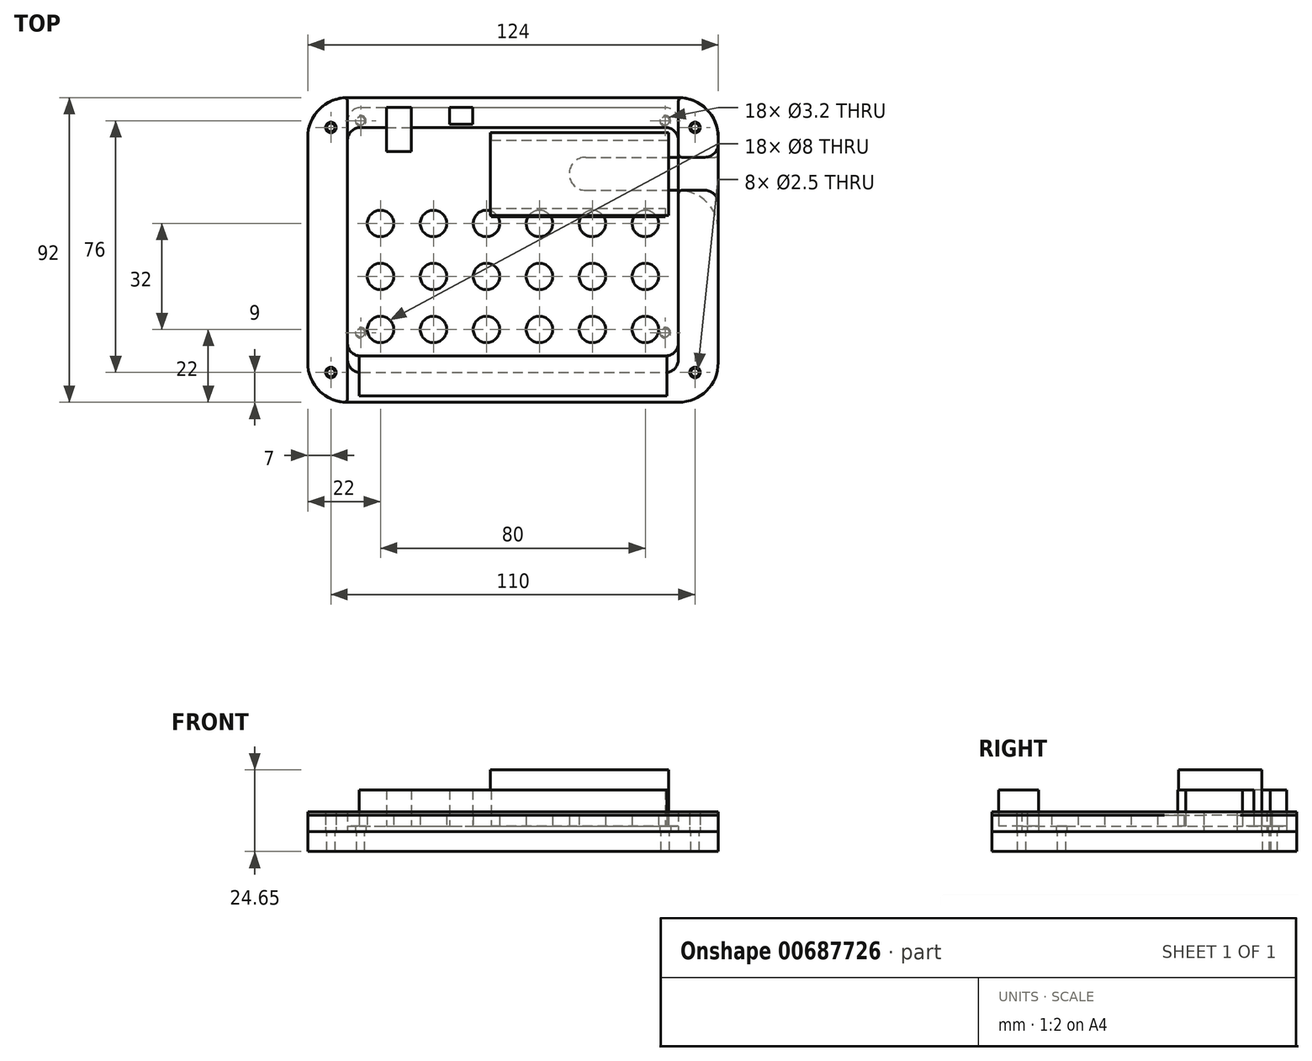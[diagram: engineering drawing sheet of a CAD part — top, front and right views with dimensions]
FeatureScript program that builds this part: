
annotation { "Feature Type Name" : "Feature", "Feature Type Description" : "" }
export const myFeature = defineFeature(function(context is Context, id is Id, definition is map)
    precondition{}
    {
        {
            var Q0;
            Q0=qCreatedBy(makeId("Top.planeOp"),FACE);
            var sketch = newSketch(context, id + "F0", { "sketchPlane" : qUnion([Q0])});
            skLineSegment(sketch, "E0.bottom", {"start": v(0, 0) * mm, "end": v(100, 0) * mm});
            skLineSegment(sketch, "E0.top", {"start": v(0, 80) * mm, "end": v(100, 80) * mm});
            skLineSegment(sketch, "E0.left", {"start": v(0, 0) * mm, "end": v(0, 80) * mm});
            skLineSegment(sketch, "E0.right", {"start": v(100, 0) * mm, "end": v(100, 80) * mm});
            skCircle(sketch, "E1", {"center": v(4, 76) * mm, "radius": 1.6 * mm});
            skCircle(sketch, "E2", {"center": v(4, 12) * mm, "radius": 1.6 * mm});
            skCircle(sketch, "E3", {"center": v(96, 76) * mm, "radius": 1.6 * mm});
            skCircle(sketch, "E4", {"center": v(96, 12) * mm, "radius": 1.6 * mm});
            skSolve(sketch);
        }
        {
            var Q0;
            Q0=makeQuery(id+"F0.imprint","IMPRINT",FACE,{"disambiguationData":[TD([[makeQuery(id+"F0.imprint","IMPRINT",EDGE,{"derivedFrom":sQuery(id+"F0.wireOp",EDGE,"E0.bottom")}),1.0]])]});
            extrude(context, id + "F1", {"entities" : qUnion([Q0]), "depth" : 1.65 * mm, "offsetDistance" : 25 * mm});
        }
        {
            var Q0;
            Q0=makeQuery(id+"F1.opExtrude","SWEPT_EDGE",EDGE,{"disambiguationData":[OSD([sQuery(id+"F0.wireOp",EDGE,"E0.top"),sQuery(id+"F0.wireOp",EDGE,"E0.left")])]});
            var Q1;
            Q1=makeQuery(id+"F1.opExtrude","SWEPT_EDGE",EDGE,{"disambiguationData":[OSD([sQuery(id+"F0.wireOp",EDGE,"E0.top"),sQuery(id+"F0.wireOp",EDGE,"E0.right")])]});
            var Q2;
            Q2=makeQuery(id+"F1.opExtrude","SWEPT_EDGE",EDGE,{"disambiguationData":[OSD([sQuery(id+"F0.wireOp",EDGE,"E0.bottom"),sQuery(id+"F0.wireOp",EDGE,"E0.right")])]});
            var Q3;
            Q3=makeQuery(id+"F1.opExtrude","SWEPT_EDGE",EDGE,{"disambiguationData":[OSD([sQuery(id+"F0.wireOp",EDGE,"E0.bottom"),sQuery(id+"F0.wireOp",EDGE,"E0.left")])]});
            fillet(context, id + "F2", {"entities" : qUnion([Q0, Q1, Q2, Q3]), "radius" : 4 * mm, "tangentPropagation" : true, "allowEdgeOverflow" : false});
        }
        {
            var Q0;
            Q0=makeQuery(id+"F1.opExtrude","CAP_FACE",FACE,{"disambiguationData":[OSD([sQuery(id+"F0.wireOp",EDGE,"E0.bottom"),sQuery(id+"F0.wireOp",EDGE,"E0.top"),sQuery(id+"F0.wireOp",EDGE,"E0.left"),sQuery(id+"F0.wireOp",EDGE,"E0.right"),sQuery(id+"F0.wireOp",EDGE,"E1"),sQuery(id+"F0.wireOp",EDGE,"E2"),sQuery(id+"F0.wireOp",EDGE,"E3"),sQuery(id+"F0.wireOp",EDGE,"E4")])],"isStart":false});
            var sketch = newSketch(context, id + "F3", { "sketchPlane" : qUnion([Q0])});
            skLineSegment(sketch, "E5.bottom", {"start": v(97, 72.5) * mm, "end": v(43.4, 72.5) * mm});
            skLineSegment(sketch, "E5.top", {"start": v(97, 70.05) * mm, "end": v(43.4, 70.05) * mm});
            skLineSegment(sketch, "E5.left", {"start": v(97, 72.5) * mm, "end": v(97, 70.05) * mm});
            skLineSegment(sketch, "E5.right", {"start": v(43.4, 72.5) * mm, "end": v(43.4, 70.05) * mm});
            skLineSegment(sketch, "E6.bottom", {"start": v(43.4, 49.55) * mm, "end": v(96, 49.55) * mm});
            skLineSegment(sketch, "E6.top", {"start": v(43.4, 47.1) * mm, "end": v(96, 47.1) * mm});
            skLineSegment(sketch, "E6.left", {"start": v(43.4, 49.55) * mm, "end": v(43.4, 47.1) * mm});
            skLineSegment(sketch, "E6.right", {"start": v(96, 49.55) * mm, "end": v(96, 47.1) * mm});
            skLineSegment(sketch, "E7.bottom", {"start": v(30.9, 80) * mm, "end": v(37.8, 80) * mm});
            skLineSegment(sketch, "E7.top", {"start": v(30.9, 75) * mm, "end": v(37.8, 75) * mm});
            skLineSegment(sketch, "E7.left", {"start": v(30.9, 80) * mm, "end": v(30.9, 75) * mm});
            skLineSegment(sketch, "E7.right", {"start": v(37.8, 80) * mm, "end": v(37.8, 75) * mm});
            skLineSegment(sketch, "E8.bottom", {"start": v(11.74, 80) * mm, "end": v(19.36, 80) * mm});
            skLineSegment(sketch, "E8.top", {"start": v(11.74, 66.69) * mm, "end": v(19.36, 66.69) * mm});
            skLineSegment(sketch, "E8.left", {"start": v(11.74, 80) * mm, "end": v(11.74, 66.69) * mm});
            skLineSegment(sketch, "E8.right", {"start": v(19.36, 80) * mm, "end": v(19.36, 66.69) * mm});
            skLineSegment(sketch, "E9.bottom", {"start": v(3.5, 5) * mm, "end": v(96.5, 5) * mm});
            skLineSegment(sketch, "E9.top", {"start": v(3.5, -7) * mm, "end": v(96.5, -7) * mm});
            skLineSegment(sketch, "E9.left", {"start": v(3.5, 5) * mm, "end": v(3.5, -7) * mm});
            skLineSegment(sketch, "E9.right", {"start": v(96.5, 5) * mm, "end": v(96.5, -7) * mm});
            skSolve(sketch);
        }
        {
            var Q0;
            Q0=makeQuery(id+"F3.imprint","IMPRINT",FACE,{"disambiguationData":[TD([[makeQuery(id+"F3.imprint","IMPRINT",EDGE,{"derivedFrom":sQuery(id+"F3.wireOp",EDGE,"E8.bottom")}),-1.0]])]});
            var Q1;
            Q1=makeQuery(id+"F3.imprint","IMPRINT",FACE,{"disambiguationData":[TD([[makeQuery(id+"F3.imprint","IMPRINT",EDGE,{"derivedFrom":sQuery(id+"F3.wireOp",EDGE,"E7.bottom")}),-1.0]])]});
            var Q2;
            Q2=makeQuery(id+"F3.imprint","IMPRINT",FACE,{"disambiguationData":[TD([[makeQuery(id+"F3.imprint","IMPRINT",EDGE,{"derivedFrom":sQuery(id+"F3.wireOp",EDGE,"E5.bottom")}),1.0]])]});
            var Q3;
            Q3=makeQuery(id+"F3.imprint","IMPRINT",FACE,{"disambiguationData":[TD([[makeQuery(id+"F3.imprint","IMPRINT",EDGE,{"derivedFrom":sQuery(id+"F3.wireOp",EDGE,"E6.bottom")}),-1.0]])]});
            var Q4;
            {var subQ1=sQuery(id+"F3.wireOp",EDGE,"E9.bottom");Q4=makeQuery(id+"F3.imprint","IMPRINT",FACE,{"disambiguationData":[TD([[makeQuery(id+"F3.imprint","IMPRINT",EDGE,{"derivedFrom":subQ1}),-1.0]])]});}
            var Q5;
            {var subQ2=sQuery(id+"F3.wireOp",EDGE,"E9.top");Q5=makeQuery(id+"F3.imprint","IMPRINT",FACE,{"disambiguationData":[TD([[makeQuery(id+"F3.imprint","IMPRINT",EDGE,{"derivedFrom":subQ2}),1.0]])]});}
            extrude(context, id + "F4", {"entities" : qUnion([Q0, Q1, Q2, Q3, Q4, Q5]), "operationType" : NewBodyOperationType.ADD, "depth" : 11 * mm, "offsetDistance" : 25 * mm});
        }
        {
            var Q0;
            Q0=qCreatedBy(makeId("Top.planeOp"),FACE);
            var sketch = newSketch(context, id + "F5", { "sketchPlane" : qUnion([Q0])});
            skLineSegment(sketch, "E10.bottom", {"start": v(-12, 83) * mm, "end": v(112, 83) * mm});
            skLineSegment(sketch, "E10.top", {"start": v(-12, -9) * mm, "end": v(112, -9) * mm});
            skLineSegment(sketch, "E10.left", {"start": v(-12, 83) * mm, "end": v(-12, -9) * mm});
            skLineSegment(sketch, "E10.right", {"start": v(112, 83) * mm, "end": v(112, -9) * mm});
            skCircle(sketch, "E11", {"center": v(4, 76) * mm, "radius": 1.25 * mm});
            skCircle(sketch, "E12", {"center": v(4, 12) * mm, "radius": 1.25 * mm});
            skCircle(sketch, "E13", {"center": v(96, 12) * mm, "radius": 1.25 * mm});
            skCircle(sketch, "E14", {"center": v(96, 76) * mm, "radius": 1.25 * mm});
            skCircle(sketch, "E15", {"center": v(-5, 74) * mm, "radius": 1.25 * mm});
            skCircle(sketch, "E16", {"center": v(-5, 0) * mm, "radius": 1.25 * mm});
            skLineSegment(sketch, "E17", {"start": v(50, 83) * mm, "end": v(50, -9) * mm, "construction": true});
            skCircle(sketch, "E18.MirrorC", {"center": v(105, 0) * mm, "radius": 1.25 * mm});
            skCircle(sketch, "E19.MirrorC", {"center": v(105, 74) * mm, "radius": 1.25 * mm});
            skSolve(sketch);
        }
        {
            var Q0;
            Q0=makeQuery(id+"F5.imprint","IMPRINT",FACE,{"disambiguationData":[TD([[makeQuery(id+"F5.imprint","IMPRINT",EDGE,{"derivedFrom":sQuery(id+"F5.wireOp",EDGE,"E10.bottom")}),-1.0]])]});
            var Q1;
            Q1=qCreatedBy(makeId("Top.planeOp"),FACE);
            extrude(context, id + "F6", {"entities" : qUnion([Q0]), "oppositeDirection" : true, "depth" : 6 * mm, "endBoundEntityFace" : qUnion([Q1]), "hasOffset" : true, "offsetDistance" : 5 * mm});
        }
        {
            var Q0;
            Q0=makeQuery(id+"F6.opExtrude","SWEPT_EDGE",EDGE,{"disambiguationData":[OSD([sQuery(id+"F5.wireOp",EDGE,"E10.bottom"),sQuery(id+"F5.wireOp",EDGE,"E10.left")])]});
            var Q1;
            Q1=makeQuery(id+"F6.opExtrude","SWEPT_EDGE",EDGE,{"disambiguationData":[OSD([sQuery(id+"F5.wireOp",EDGE,"E10.top"),sQuery(id+"F5.wireOp",EDGE,"E10.left")])]});
            var Q2;
            Q2=makeQuery(id+"F6.opExtrude","SWEPT_EDGE",EDGE,{"disambiguationData":[OSD([sQuery(id+"F5.wireOp",EDGE,"E10.top"),sQuery(id+"F5.wireOp",EDGE,"E10.right")])]});
            var Q3;
            Q3=makeQuery(id+"F6.opExtrude","SWEPT_EDGE",EDGE,{"disambiguationData":[OSD([sQuery(id+"F5.wireOp",EDGE,"E10.bottom"),sQuery(id+"F5.wireOp",EDGE,"E10.right")])]});
            fillet(context, id + "F7", {"entities" : qUnion([Q0, Q1, Q2, Q3]), "radius" : 12 * mm, "tangentPropagation" : true, "allowEdgeOverflow" : false});
        }
        {
            var Q0;
            Q0=makeQuery(id+"F4.opExtrude","CAP_FACE",FACE,{"disambiguationData":[OSD([sQuery(id+"F3.wireOp",EDGE,"E5.bottom"),sQuery(id+"F3.wireOp",EDGE,"E5.top"),sQuery(id+"F3.wireOp",EDGE,"E5.left"),sQuery(id+"F3.wireOp",EDGE,"E5.right")])],"isStart":false});
            var sketch = newSketch(context, id + "F8", { "sketchPlane" : qUnion([Q0])});
            skLineSegment(sketch, "E20.bottom", {"start": v(97, 72.5) * mm, "end": v(43.24, 72.5) * mm});
            skLineSegment(sketch, "E20.top", {"start": v(97, 47.4) * mm, "end": v(43.24, 47.4) * mm});
            skLineSegment(sketch, "E20.left", {"start": v(97, 72.5) * mm, "end": v(97, 47.4) * mm});
            skLineSegment(sketch, "E20.right", {"start": v(43.24, 72.5) * mm, "end": v(43.24, 47.4) * mm});
            skSolve(sketch);
        }
        {
            var Q0;
            {var subQ3=sQuery(id+"F8.wireOp",EDGE,"E20.top");Q0=makeQuery(id+"F8.imprint","IMPRINT",FACE,{"disambiguationData":[TD([[makeQuery(id+"F8.imprint","IMPRINT",EDGE,{"derivedFrom":subQ3}),-1.0]])]});}
            var Q1;
            {var subQ4=makeQuery(id+"F4.opExtrude","CAP_EDGE",EDGE,{"disambiguationData":[OSD([sQuery(id+"F3.wireOp",EDGE,"E5.top")])],"isStart":false});Q1=makeQuery(id+"F8.imprint","IMPRINT",FACE,{"disambiguationData":[TD([[makeQuery(id+"F8.imprint","IMPRINT",EDGE,{"derivedFrom":subQ4}),-1.0]])]});}
            extrude(context, id + "F9", {"entities" : qUnion([Q0, Q1]), "operationType" : NewBodyOperationType.ADD, "depth" : 6 * mm, "offsetDistance" : 25 * mm});
        }
        {
            var Q0;
            Q0=qCreatedBy(makeId("Top.planeOp"),FACE);
            var sketch = newSketch(context, id + "F10", { "sketchPlane" : qUnion([Q0])});
            skLineSegment(sketch, "E21.bottom", {"start": v(0, 83) * mm, "end": v(-12, 83) * mm});
            skLineSegment(sketch, "E21.top", {"start": v(0, -9) * mm, "end": v(-12, -9) * mm});
            skLineSegment(sketch, "E21.left", {"start": v(0, 83) * mm, "end": v(0, -9) * mm});
            skLineSegment(sketch, "E21.right", {"start": v(-12, 83) * mm, "end": v(-12, -9) * mm});
            skCircle(sketch, "E22", {"center": v(-5, 74) * mm, "radius": 1.6 * mm});
            skCircle(sketch, "E23", {"center": v(-5, 0) * mm, "radius": 1.6 * mm});
            skSolve(sketch);
        }
        {
            var Q0;
            Q0=makeQuery(id+"F10.imprint","IMPRINT",FACE,{"disambiguationData":[TD([[makeQuery(id+"F10.imprint","IMPRINT",EDGE,{"derivedFrom":sQuery(id+"F10.wireOp",EDGE,"E21.bottom")}),1.0]])]});
            extrude(context, id + "F11", {"entities" : qUnion([Q0]), "depth" : 6 * mm, "offsetDistance" : 25 * mm});
        }
        {
            var Q0;
            Q0=makeQuery(id+"F11.opExtrude","SWEPT_EDGE",EDGE,{"disambiguationData":[OSD([sQuery(id+"F10.wireOp",EDGE,"E21.top"),sQuery(id+"F10.wireOp",EDGE,"E21.right")])]});
            var Q1;
            Q1=makeQuery(id+"F11.opExtrude","SWEPT_EDGE",EDGE,{"disambiguationData":[OSD([sQuery(id+"F10.wireOp",EDGE,"E21.bottom"),sQuery(id+"F10.wireOp",EDGE,"E21.right")])]});
            fillet(context, id + "F12", {"entities" : qUnion([Q0, Q1]), "radius" : 12 * mm, "tangentPropagation" : true, "allowEdgeOverflow" : false});
        }
        {
            var Q0;
            Q0=makeQuery(id+"F12.opFillet","BLEND_EDGE",EDGE,{"blendedFrom":[makeQuery(id+"F11.opExtrude","SWEPT_EDGE",EDGE,{"disambiguationData":[OSD([sQuery(id+"F10.wireOp",EDGE,"E21.bottom"),sQuery(id+"F10.wireOp",EDGE,"E21.right")])]}),makeQuery(id+"F11.opExtrude","SWEPT_FACE",FACE,{"disambiguationData":[OSD([sQuery(id+"F10.wireOp",EDGE,"E21.left")])]})],"blendedInto":[makeQuery(id+"F11.opExtrude","SWEPT_FACE",FACE,{"disambiguationData":[OSD([sQuery(id+"F10.wireOp",EDGE,"E21.left")])]})]});
            var Q1;
            Q1=makeQuery(id+"F12.opFillet","BLEND_EDGE",EDGE,{"blendedFrom":[makeQuery(id+"F11.opExtrude","SWEPT_EDGE",EDGE,{"disambiguationData":[OSD([sQuery(id+"F10.wireOp",EDGE,"E21.top"),sQuery(id+"F10.wireOp",EDGE,"E21.right")])]}),makeQuery(id+"F11.opExtrude","SWEPT_FACE",FACE,{"disambiguationData":[OSD([sQuery(id+"F10.wireOp",EDGE,"E21.left")])]})],"blendedInto":[makeQuery(id+"F11.opExtrude","SWEPT_FACE",FACE,{"disambiguationData":[OSD([sQuery(id+"F10.wireOp",EDGE,"E21.left")])]})]});
            fillet(context, id + "F13", {"entities" : qUnion([Q0, Q1]), "radius" : 1 * mm, "tangentPropagation" : true, "allowEdgeOverflow" : false});
        }
        {
            var Q0;
            Q0=qCreatedBy(makeId("Top.planeOp"),FACE);
            var sketch = newSketch(context, id + "F14", { "sketchPlane" : qUnion([Q0])});
            skLineSegment(sketch, "E24.bottom", {"start": v(-12, 83) * mm, "end": v(112, 83) * mm});
            skLineSegment(sketch, "E24.top", {"start": v(-12, -9) * mm, "end": v(112, -9) * mm});
            skLineSegment(sketch, "E24.left", {"start": v(-12, 83) * mm, "end": v(-12, -9) * mm});
            skLineSegment(sketch, "E24.right", {"start": v(112, 83) * mm, "end": v(112, 65) * mm});
            skLineSegment(sketch, "E25.bottom", {"start": v(0, 74) * mm, "end": v(100, 74) * mm});
            skLineSegment(sketch, "E25.top", {"start": v(0, 5) * mm, "end": v(100, 5) * mm});
            skLineSegment(sketch, "E25.left", {"start": v(0, 74) * mm, "end": v(0, 5) * mm});
            skLineSegment(sketch, "E25.right", {"start": v(100, 74) * mm, "end": v(100, 65) * mm});
            skCircle(sketch, "E26", {"center": v(-5, 74) * mm, "radius": 1.6 * mm});
            skCircle(sketch, "E27", {"center": v(-5, 0) * mm, "radius": 1.6 * mm});
            skLineSegment(sketch, "E28", {"start": v(50, 83) * mm, "end": v(50, -9) * mm, "construction": true});
            skCircle(sketch, "E29.MirrorC", {"center": v(105, 0) * mm, "radius": 1.6 * mm});
            skCircle(sketch, "E30.MirrorC", {"center": v(105, 74) * mm, "radius": 1.6 * mm});
            skLineSegment(sketch, "E31", {"start": v(112, 65) * mm, "end": v(100, 65) * mm});
            skLineSegment(sketch, "E32", {"start": v(112, 55) * mm, "end": v(100, 55) * mm});
            skLineSegment(sketch, "E33.trimOffspring", {"start": v(112, 55) * mm, "end": v(112, -9) * mm});
            skLineSegment(sketch, "E34.trimOffspring", {"start": v(100, 55) * mm, "end": v(100, 5) * mm});
            skSolve(sketch);
        }
        {
            var Q0;
            Q0 = qSketchRegion(id + "F14", true);
            extrude(context, id + "F15", {"entities" : qUnion([Q0]), "depth" : 6 * mm, "offsetDistance" : 25 * mm});
        }
        {
            var Q0;
            Q0=makeQuery(id+"F15.opExtrude","SWEPT_EDGE",EDGE,{"disambiguationData":[OSD([sQuery(id+"F14.wireOp",EDGE,"E24.top"),sQuery(id+"F14.wireOp",EDGE,"E24.left")])]});
            var Q1;
            Q1=makeQuery(id+"F15.opExtrude","SWEPT_EDGE",EDGE,{"disambiguationData":[OSD([sQuery(id+"F14.wireOp",EDGE,"E24.top"),sQuery(id+"F14.wireOp",EDGE,"E33.trimOffspring")])]});
            var Q2;
            Q2=makeQuery(id+"F15.opExtrude","SWEPT_EDGE",EDGE,{"disambiguationData":[OSD([sQuery(id+"F14.wireOp",EDGE,"E24.bottom"),sQuery(id+"F14.wireOp",EDGE,"E24.right")])]});
            var Q3;
            Q3=makeQuery(id+"F15.opExtrude","SWEPT_EDGE",EDGE,{"disambiguationData":[OSD([sQuery(id+"F14.wireOp",EDGE,"E24.bottom"),sQuery(id+"F14.wireOp",EDGE,"E24.left")])]});
            fillet(context, id + "F16", {"entities" : qUnion([Q0, Q1, Q2, Q3]), "radius" : 12 * mm, "tangentPropagation" : true, "allowEdgeOverflow" : false});
        }
        {
            var Q0;
            Q0=makeQuery(id+"F15.opExtrude","SWEPT_EDGE",EDGE,{"disambiguationData":[OSD([sQuery(id+"F14.wireOp",EDGE,"E25.bottom"),sQuery(id+"F14.wireOp",EDGE,"E25.right")])]});
            var Q1;
            Q1=makeQuery(id+"F15.opExtrude","SWEPT_EDGE",EDGE,{"disambiguationData":[OSD([sQuery(id+"F14.wireOp",EDGE,"E25.top"),sQuery(id+"F14.wireOp",EDGE,"E25.left")])]});
            var Q2;
            Q2=makeQuery(id+"F15.opExtrude","SWEPT_EDGE",EDGE,{"disambiguationData":[OSD([sQuery(id+"F14.wireOp",EDGE,"E25.top"),sQuery(id+"F14.wireOp",EDGE,"E34.trimOffspring")])]});
            var Q3;
            Q3=makeQuery(id+"F15.opExtrude","SWEPT_EDGE",EDGE,{"disambiguationData":[OSD([sQuery(id+"F14.wireOp",EDGE,"E25.bottom"),sQuery(id+"F14.wireOp",EDGE,"E25.left")])]});
            fillet(context, id + "F17", {"entities" : qUnion([Q0, Q1, Q2, Q3]), "radius" : 4 * mm, "tangentPropagation" : true, "allowEdgeOverflow" : false});
        }
        {
            var Q0;
            Q0=qCreatedBy(makeId("Top.planeOp"),FACE);
            var sketch = newSketch(context, id + "F18", { "sketchPlane" : qUnion([Q0])});
            skLineSegment(sketch, "E35.bottom", {"start": v(-12, -9) * mm, "end": v(112, -9) * mm});
            skLineSegment(sketch, "E35.top", {"start": v(-12, 83) * mm, "end": v(112, 83) * mm});
            skLineSegment(sketch, "E35.left", {"start": v(-12, -9) * mm, "end": v(-12, 83) * mm});
            skLineSegment(sketch, "E35.right", {"start": v(112, -9) * mm, "end": v(112, 55) * mm});
            skCircle(sketch, "E36", {"center": v(-5, 0) * mm, "radius": 1.6 * mm});
            skCircle(sketch, "E37", {"center": v(-5, 74) * mm, "radius": 1.6 * mm});
            skLineSegment(sketch, "E38", {"start": v(50, 83) * mm, "end": v(50, -9) * mm, "construction": true});
            skCircle(sketch, "E39.MirrorC", {"center": v(105, 0) * mm, "radius": 1.6 * mm});
            skCircle(sketch, "E40.MirrorC", {"center": v(105, 74) * mm, "radius": 1.6 * mm});
            skLineSegment(sketch, "E41", {"start": v(72, 60) * mm, "end": v(112, 60) * mm, "construction": true});
            skArc(sketch, "E42.0.startCap", {"start": v(72, 55) * mm, "mid": v(67, 60) * mm, "end": v(72, 65) * mm});
            skArc(sketch, "E42.0.endCap", {"start": v(112, 65) * mm, "mid": v(117, 60) * mm, "end": v(112, 55) * mm, "construction": true});
            skLineSegment(sketch, "E42.0.left", {"start": v(72, 65) * mm, "end": v(112, 65) * mm});
            skLineSegment(sketch, "E42.0.right", {"start": v(72, 55) * mm, "end": v(112, 55) * mm});
            skLineSegment(sketch, "E43.trimOffspring", {"start": v(112, 65) * mm, "end": v(112, 83) * mm});
            skCircle(sketch, "E44", {"center": v(10, 13) * mm, "radius": 4 * mm});
            skCircle(sketch, "E45.0.1.0", {"center": v(10, 29) * mm, "radius": 4 * mm});
            skCircle(sketch, "E45.0.2.0", {"center": v(10, 45) * mm, "radius": 4 * mm});
            skCircle(sketch, "E45.1.0.0", {"center": v(26, 13) * mm, "radius": 4 * mm});
            skCircle(sketch, "E45.1.1.0", {"center": v(26, 29) * mm, "radius": 4 * mm});
            skCircle(sketch, "E45.1.2.0", {"center": v(26, 45) * mm, "radius": 4 * mm});
            skCircle(sketch, "E45.2.0.0", {"center": v(42, 13) * mm, "radius": 4 * mm});
            skCircle(sketch, "E45.2.1.0", {"center": v(42, 29) * mm, "radius": 4 * mm});
            skCircle(sketch, "E45.2.2.0", {"center": v(42, 45) * mm, "radius": 4 * mm});
            skCircle(sketch, "E45.3.0.0", {"center": v(58, 13) * mm, "radius": 4 * mm});
            skCircle(sketch, "E45.3.1.0", {"center": v(58, 29) * mm, "radius": 4 * mm});
            skCircle(sketch, "E45.3.2.0", {"center": v(58, 45) * mm, "radius": 4 * mm});
            skCircle(sketch, "E45.4.0.0", {"center": v(74, 13) * mm, "radius": 4 * mm});
            skCircle(sketch, "E45.4.1.0", {"center": v(74, 29) * mm, "radius": 4 * mm});
            skCircle(sketch, "E45.4.2.0", {"center": v(74, 45) * mm, "radius": 4 * mm});
            skCircle(sketch, "E45.5.0.0", {"center": v(90, 13) * mm, "radius": 4 * mm});
            skCircle(sketch, "E45.5.1.0", {"center": v(90, 29) * mm, "radius": 4 * mm});
            skCircle(sketch, "E45.5.2.0", {"center": v(90, 45) * mm, "radius": 4 * mm});
            skLineSegment(sketch, "E45.direction1", {"start": v(10, 13) * mm, "end": v(26, 13) * mm, "construction": true});
            skLineSegment(sketch, "E45.direction2", {"start": v(10, 13) * mm, "end": v(10, 29) * mm, "construction": true});
            skSolve(sketch);
        }
        {
            var Q0;
            Q0=makeQuery(id+"F18.imprint","IMPRINT",FACE,{"disambiguationData":[TD([[makeQuery(id+"F18.imprint","IMPRINT",EDGE,{"derivedFrom":sQuery(id+"F18.wireOp",EDGE,"E35.bottom")}),1.0]])]});
            extrude(context, id + "F19", {"entities" : qUnion([Q0]), "depth" : 5 * mm, "offsetDistance" : 25 * mm});
        }
        {
            var Q0;
            Q0=makeQuery(id+"F19.opExtrude","SWEPT_EDGE",EDGE,{"disambiguationData":[OSD([sQuery(id+"F18.wireOp",EDGE,"E35.bottom"),sQuery(id+"F18.wireOp",EDGE,"E35.left")])]});
            var Q1;
            Q1=makeQuery(id+"F19.opExtrude","SWEPT_EDGE",EDGE,{"disambiguationData":[OSD([sQuery(id+"F18.wireOp",EDGE,"E35.top"),sQuery(id+"F18.wireOp",EDGE,"E35.left")])]});
            var Q2;
            Q2=makeQuery(id+"F19.opExtrude","SWEPT_EDGE",EDGE,{"disambiguationData":[OSD([sQuery(id+"F18.wireOp",EDGE,"E35.bottom"),sQuery(id+"F18.wireOp",EDGE,"E35.right")])]});
            var Q3;
            Q3=makeQuery(id+"F19.opExtrude","SWEPT_EDGE",EDGE,{"disambiguationData":[OSD([sQuery(id+"F18.wireOp",EDGE,"E35.top"),sQuery(id+"F18.wireOp",EDGE,"E35.right")])]});
            fillet(context, id + "F20", {"entities" : qUnion([Q0, Q1, Q2, Q3]), "radius" : 12 * mm, "tangentPropagation" : true, "allowEdgeOverflow" : false});
        }
        {
            var Q0;
            Q0=qCreatedBy(makeId("Top.planeOp"),FACE);
            var sketch = newSketch(context, id + "F21", { "sketchPlane" : qUnion([Q0])});
            skLineSegment(sketch, "E46.bottom", {"start": v(-12, 83) * mm, "end": v(0, 83) * mm});
            skLineSegment(sketch, "E46.top", {"start": v(-12, -9) * mm, "end": v(112, -9) * mm});
            skLineSegment(sketch, "E46.left", {"start": v(-12, 83) * mm, "end": v(-12, -9) * mm});
            skLineSegment(sketch, "E46.right", {"start": v(112, 83) * mm, "end": v(112, -9) * mm});
            skLineSegment(sketch, "E47", {"start": v(0, 83) * mm, "end": v(0, 0) * mm});
            skLineSegment(sketch, "E48", {"start": v(0, 0) * mm, "end": v(100, 0) * mm});
            skLineSegment(sketch, "E49", {"start": v(100, 0) * mm, "end": v(100, 83) * mm});
            skLineSegment(sketch, "E50.trimOffspring", {"start": v(100, 83) * mm, "end": v(112, 83) * mm});
            skCircle(sketch, "E51", {"center": v(-5, 74) * mm, "radius": 1.6 * mm});
            skCircle(sketch, "E52", {"center": v(-5, 0) * mm, "radius": 1.6 * mm});
            skLineSegment(sketch, "E53", {"start": v(50, -9) * mm, "end": v(50, 82.85) * mm, "construction": true});
            skCircle(sketch, "E54.MirrorC", {"center": v(105, 0) * mm, "radius": 1.6 * mm});
            skCircle(sketch, "E55.MirrorC", {"center": v(105, 74) * mm, "radius": 1.6 * mm});
            skSolve(sketch);
        }
        {
            var Q0;
            Q0 = qSketchRegion(id + "F21", true);
            extrude(context, id + "F22", {"entities" : qUnion([Q0]), "depth" : 6 * mm, "offsetDistance" : 25 * mm});
        }
        {
            var Q0;
            Q0=makeQuery(id+"F22.opExtrude","SWEPT_EDGE",EDGE,{"disambiguationData":[OSD([sQuery(id+"F21.wireOp",EDGE,"E46.top"),sQuery(id+"F21.wireOp",EDGE,"E46.left")])]});
            var Q1;
            Q1=makeQuery(id+"F22.opExtrude","SWEPT_EDGE",EDGE,{"disambiguationData":[OSD([sQuery(id+"F21.wireOp",EDGE,"E46.top"),sQuery(id+"F21.wireOp",EDGE,"E46.right")])]});
            var Q2;
            Q2=makeQuery(id+"F22.opExtrude","SWEPT_EDGE",EDGE,{"disambiguationData":[OSD([sQuery(id+"F21.wireOp",EDGE,"E46.right"),sQuery(id+"F21.wireOp",EDGE,"E50.trimOffspring")])]});
            var Q3;
            Q3=makeQuery(id+"F22.opExtrude","SWEPT_EDGE",EDGE,{"disambiguationData":[OSD([sQuery(id+"F21.wireOp",EDGE,"E46.bottom"),sQuery(id+"F21.wireOp",EDGE,"E46.left")])]});
            fillet(context, id + "F23", {"entities" : qUnion([Q0, Q1, Q2, Q3]), "radius" : 12 * mm, "tangentPropagation" : true, "allowEdgeOverflow" : false});
        }
        {
            var Q0;
            Q0=makeQuery(id+"F22.opExtrude","SWEPT_EDGE",EDGE,{"disambiguationData":[OSD([sQuery(id+"F21.wireOp",EDGE,"E47"),sQuery(id+"F21.wireOp",EDGE,"E48")])]});
            var Q1;
            Q1=makeQuery(id+"F22.opExtrude","SWEPT_EDGE",EDGE,{"disambiguationData":[OSD([sQuery(id+"F21.wireOp",EDGE,"E48"),sQuery(id+"F21.wireOp",EDGE,"E49")])]});
            fillet(context, id + "F24", {"entities" : qUnion([Q0, Q1]), "radius" : 4 * mm, "tangentPropagation" : true, "allowEdgeOverflow" : false});
        }
        {
            var Q0;
            Q0=makeQuery(id+"F23.opFillet","BLEND_EDGE",EDGE,{"blendedFrom":[makeQuery(id+"F22.opExtrude","SWEPT_EDGE",EDGE,{"disambiguationData":[OSD([sQuery(id+"F21.wireOp",EDGE,"E46.right"),sQuery(id+"F21.wireOp",EDGE,"E50.trimOffspring")])]}),makeQuery(id+"F22.opExtrude","SWEPT_FACE",FACE,{"disambiguationData":[OSD([sQuery(id+"F21.wireOp",EDGE,"E49")])]})],"blendedInto":[makeQuery(id+"F22.opExtrude","SWEPT_FACE",FACE,{"disambiguationData":[OSD([sQuery(id+"F21.wireOp",EDGE,"E49")])]})]});
            var Q1;
            Q1=makeQuery(id+"F23.opFillet","BLEND_EDGE",EDGE,{"blendedFrom":[makeQuery(id+"F22.opExtrude","SWEPT_EDGE",EDGE,{"disambiguationData":[OSD([sQuery(id+"F21.wireOp",EDGE,"E46.bottom"),sQuery(id+"F21.wireOp",EDGE,"E46.left")])]}),makeQuery(id+"F22.opExtrude","SWEPT_FACE",FACE,{"disambiguationData":[OSD([sQuery(id+"F21.wireOp",EDGE,"E47")])]})],"blendedInto":[makeQuery(id+"F22.opExtrude","SWEPT_FACE",FACE,{"disambiguationData":[OSD([sQuery(id+"F21.wireOp",EDGE,"E47")])]})]});
            fillet(context, id + "F25", {"entities" : qUnion([Q0, Q1]), "radius" : 1 * mm, "tangentPropagation" : true, "allowEdgeOverflow" : false});
        }
        {
            var Q0;
            Q0=makeQuery(id+"F19.opExtrude","SWEPT_EDGE",EDGE,{"disambiguationData":[OSD([sQuery(id+"F18.wireOp",EDGE,"E42.0.left"),sQuery(id+"F18.wireOp",EDGE,"E43.trimOffspring")])]});
            var Q1;
            Q1=makeQuery(id+"F19.opExtrude","SWEPT_EDGE",EDGE,{"disambiguationData":[OSD([sQuery(id+"F18.wireOp",EDGE,"E35.right"),sQuery(id+"F18.wireOp",EDGE,"E42.0.right")])]});
            fillet(context, id + "F26", {"entities" : qUnion([Q0, Q1]), "radius" : 1 * mm, "tangentPropagation" : true, "allowEdgeOverflow" : false});
        }
        {
            var Q0;
            Q0=makeQuery(id+"F15.opExtrude","SWEPT_EDGE",EDGE,{"disambiguationData":[OSD([sQuery(id+"F14.wireOp",EDGE,"E25.right"),sQuery(id+"F14.wireOp",EDGE,"E31")])]});
            var Q1;
            Q1=makeQuery(id+"F15.opExtrude","SWEPT_EDGE",EDGE,{"disambiguationData":[OSD([sQuery(id+"F14.wireOp",EDGE,"E32"),sQuery(id+"F14.wireOp",EDGE,"E34.trimOffspring")])]});
            fillet(context, id + "F27", {"entities" : qUnion([Q0, Q1]), "radius" : 1 * mm, "tangentPropagation" : true, "allowEdgeOverflow" : false});
        }
        {
            var Q0;
            Q0=makeQuery(id+"F15.opExtrude","SWEPT_EDGE",EDGE,{"disambiguationData":[OSD([sQuery(id+"F14.wireOp",EDGE,"E24.right"),sQuery(id+"F14.wireOp",EDGE,"E31")])]});
            var Q1;
            Q1=makeQuery(id+"F15.opExtrude","SWEPT_EDGE",EDGE,{"disambiguationData":[OSD([sQuery(id+"F14.wireOp",EDGE,"E32"),sQuery(id+"F14.wireOp",EDGE,"E33.trimOffspring")])]});
            fillet(context, id + "F28", {"entities" : qUnion([Q0, Q1]), "radius" : 4 * mm, "tangentPropagation" : true, "allowEdgeOverflow" : false});
        }
    });
